# Revit family: Portinhola Correr
name_source: partatom
category: Doors
units: mm (PartAtom-declared; Revit-internal decimal feet)

## family parameters
Cut with Voids When Loaded = Yes
Host = Face
Room Calculation Point = No
Shared = No

## types (2) — shared parameters
Altura trilho superior = 390 mm  [stored 1.27953 ft]
Automatica = No
Define Thermal Properties by = Schematic Type
Dist Motor = 30 mm  [stored 0.0984252 ft]
Manual = Yes
zero-valued in all types: Default Elevation

## per-type parameters (varying)
| type | Altura Vao Luz | Height | Largura Vao Luz | Thickness | Width |
| 1000 x 2200 x 150 mm | 2200 mm | 2200 mm | 1000 mm  [stored 3.28084 ft] | 150 mm  [stored 0.492126 ft] | 1000 mm  [stored 3.28084 ft] |
| 2000 x 2500 x 100 mm | 800 mm  [stored 2.62467 ft] | 800 mm  [stored 2.62467 ft] | 800 mm  [stored 2.62467 ft] | 100 mm  [stored 0.328084 ft] | 800 mm  [stored 2.62467 ft] |

note: [stored X ft] marks values corroborated as IEEE doubles in the binary element streams (Revit-internal decimal feet)

## geometry (parser evidence)
native form markers: Blend x2
no freeform markers — native parametric forms only
